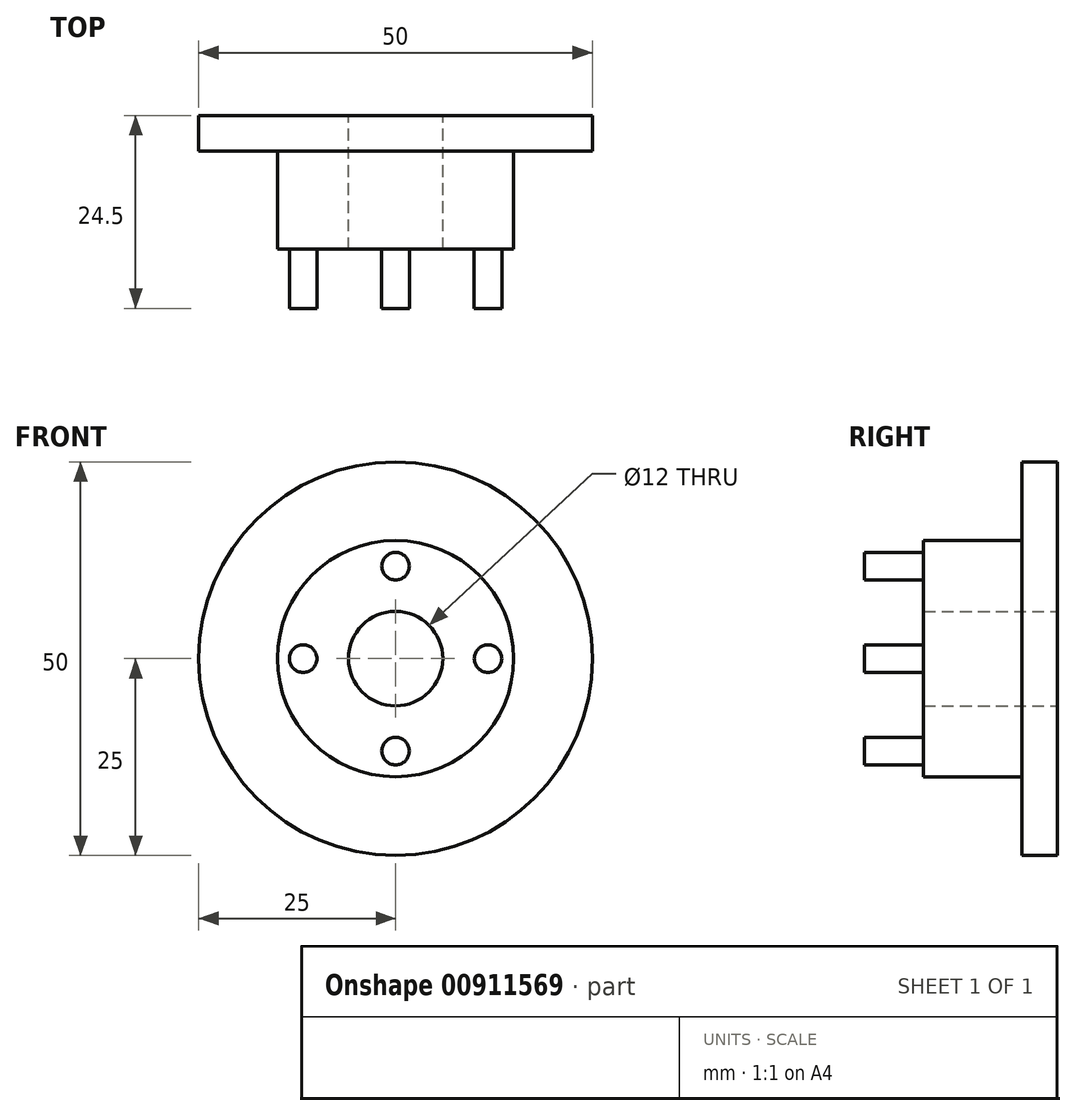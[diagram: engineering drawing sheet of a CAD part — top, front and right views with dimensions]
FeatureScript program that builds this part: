
annotation { "Feature Type Name" : "Feature", "Feature Type Description" : "" }
export const myFeature = defineFeature(function(context is Context, id is Id, definition is map)
    precondition{}
    {
        {
            var Q0;
            Q0=qCreatedBy(makeId("Front.planeOp"),FACE);
            var sketch = newSketch(context, id + "F0", { "sketchPlane" : qUnion([Q0])});
            skCircle(sketch, "E0", {"center": v(0, 0) * mm, "radius": 15 * mm});
            skCircle(sketch, "E1", {"center": v(0, 0) * mm, "radius": 6 * mm});
            skSolve(sketch);
        }
        {
            var Q0;
            Q0 = qSketchRegion(id + "F0", true);
            extrude(context, id + "F1", {"entities" : qUnion([Q0]), "depth" : 12.5 * mm, "offsetDistance" : 25 * mm});
        }
        {
            var Q0;
            Q0=makeQuery(id+"F1.opExtrude","CAP_FACE",FACE,{"disambiguationData":[OSD([sQuery(id+"F0.wireOp",EDGE,"E0")])],"isStart":false});
            var sketch = newSketch(context, id + "F2", { "sketchPlane" : qUnion([Q0])});
            skCircle(sketch, "E2", {"center": v(0, 0) * mm, "radius": 15 * mm});
            skSolve(sketch);
        }
        {
            var Q0;
            Q0=makeQuery(id+"F1.opExtrude","CAP_FACE",FACE,{"disambiguationData":[OSD([sQuery(id+"F0.wireOp",EDGE,"E0")])],"isStart":true});
            var sketch = newSketch(context, id + "F3", { "sketchPlane" : qUnion([Q0])});
            skCircle(sketch, "E3", {"center": v(0, 0) * mm, "radius": 25 * mm});
            skCircle(sketch, "E4", {"center": v(0, 0) * mm, "radius": 6 * mm});
            skSolve(sketch);
        }
        {
            var Q0;
            Q0 = qSketchRegion(id + "F3", true);
            extrude(context, id + "F4", {"entities" : qUnion([Q0]), "operationType" : NewBodyOperationType.ADD, "depth" : 4.5 * mm, "offsetDistance" : 25 * mm});
        }
        {
            var Q0;
            Q0=makeQuery(id+"F2.imprint","IMPRINT",FACE,{"disambiguationData":[TD([[makeQuery(id+"F2.imprint","IMPRINT",EDGE,{"derivedFrom":sQuery(id+"F2.wireOp",EDGE,"E2")}),1.0]])]});
            var sketch = newSketch(context, id + "F5", { "sketchPlane" : qUnion([Q0])});
            skCircle(sketch, "E5", {"center": v(0, 11.74) * mm, "radius": 1.75 * mm});
            skCircle(sketch, "E6", {"center": v(-11.74, 0) * mm, "radius": 1.75 * mm});
            skCircle(sketch, "E7", {"center": v(11.74, 0) * mm, "radius": 1.75 * mm});
            skCircle(sketch, "E8", {"center": v(0, -11.74) * mm, "radius": 1.75 * mm});
            skSolve(sketch);
        }
        {
            var Q0;
            Q0 = qSketchRegion(id + "F5", true);
            extrude(context, id + "F6", {"entities" : qUnion([Q0]), "operationType" : NewBodyOperationType.ADD, "depth" : 7.5 * mm, "offsetDistance" : 25 * mm});
        }
    });
